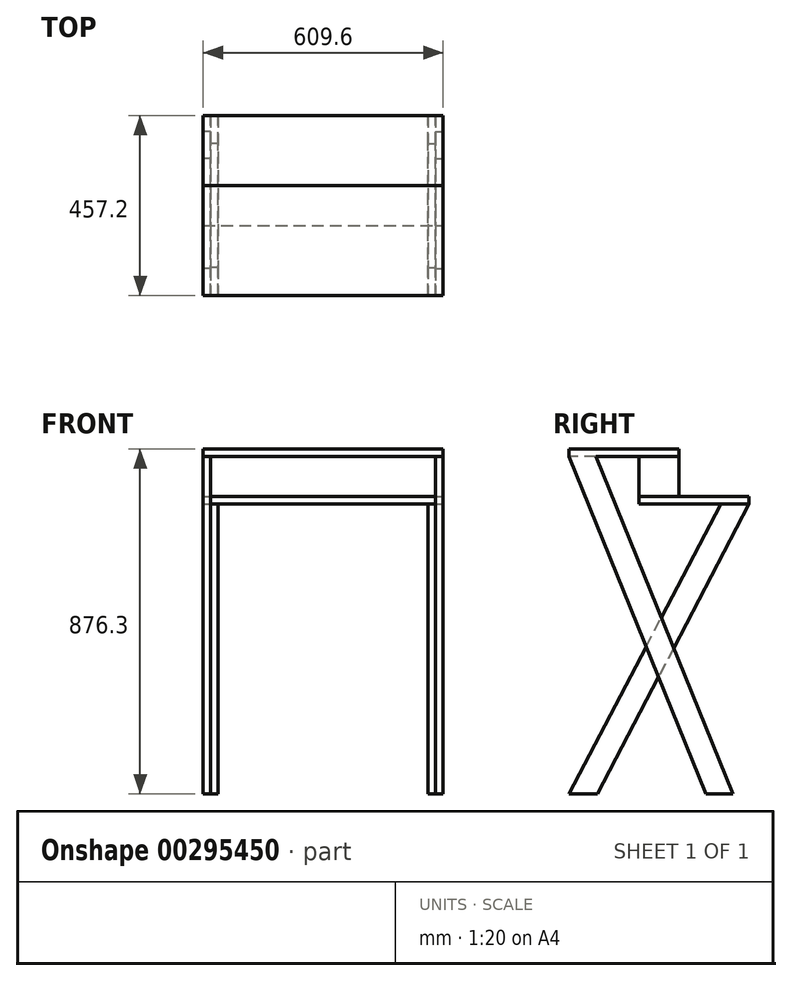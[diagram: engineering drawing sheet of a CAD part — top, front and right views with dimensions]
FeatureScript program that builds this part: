
annotation { "Feature Type Name" : "Feature", "Feature Type Description" : "" }
export const myFeature = defineFeature(function(context is Context, id is Id, definition is map)
    precondition{}
    {
        {
            var Q0;
            Q0=qCreatedBy(makeId("Top.planeOp"),FACE);
            var sketch = newSketch(context, id + "F0", { "sketchPlane" : qUnion([Q0])});
            skLineSegment(sketch, "E0.bottom", {"start": v(0, 0) * mm, "end": v(609.6, 0) * mm});
            skLineSegment(sketch, "E0.top", {"start": v(0, 279.4) * mm, "end": v(609.6, 279.4) * mm});
            skLineSegment(sketch, "E0.left", {"start": v(0, 0) * mm, "end": v(0, 279.4) * mm});
            skLineSegment(sketch, "E0.right", {"start": v(609.6, 0) * mm, "end": v(609.6, 279.4) * mm});
            skSolve(sketch);
        }
        {
            var Q0;
            Q0=makeQuery(id+"F0.imprint","IMPRINT",FACE,{"disambiguationData":[TD([[makeQuery(id+"F0.imprint","IMPRINT",EDGE,{"derivedFrom":sQuery(id+"F0.wireOp",EDGE,"E0.bottom")}),1.0]])]});
            extrude(context, id + "F1", {"entities" : qUnion([Q0]), "depth" : 19.05 * mm});
        }
        {
            var Q0;
            Q0=qCreatedBy(makeId("Top.planeOp"),FACE);
            cPlane(context, id + "F2", {"entities" : qUnion([Q0]), "cplaneType" : CPlaneType.OFFSET, "offset" : 120.65 * mm, "width" : 152.4 * mm, "height" : 152.4 * mm});
        }
        {
            var Q0;
            Q0=qCreatedBy(id+"F2.planeOp",FACE);
            var sketch = newSketch(context, id + "F3", { "sketchPlane" : qUnion([Q0])});
            skLineSegment(sketch, "E1.bottom", {"start": v(0, 101.6) * mm, "end": v(609.6, 101.6) * mm});
            skLineSegment(sketch, "E1.top", {"start": v(0, -177.8) * mm, "end": v(609.6, -177.8) * mm});
            skLineSegment(sketch, "E1.left", {"start": v(0, 101.6) * mm, "end": v(0, -177.8) * mm});
            skLineSegment(sketch, "E1.right", {"start": v(609.6, 101.6) * mm, "end": v(609.6, -177.8) * mm});
            skSolve(sketch);
        }
        {
            var Q0;
            Q0=makeQuery(id+"F3.imprint","IMPRINT",FACE,{"disambiguationData":[TD([[makeQuery(id+"F3.imprint","IMPRINT",EDGE,{"derivedFrom":sQuery(id+"F3.wireOp",EDGE,"E1.bottom")}),-1.0]])]});
            extrude(context, id + "F4", {"entities" : qUnion([Q0]), "depth" : 19.05 * mm});
        }
        {
            var Q0;
            Q0=makeQuery(id+"F4.opExtrude","SWEPT_FACE",FACE,{"disambiguationData":[OSD([sQuery(id+"F3.wireOp",EDGE,"E1.left")])]});
            var sketch = newSketch(context, id + "F5", { "sketchPlane" : qUnion([Q0])});
            skLineSegment(sketch, "E2", {"start": v(177.8, 120.65) * mm, "end": v(-170.08, -736.6) * mm});
            skLineSegment(sketch, "E3", {"start": v(-238.6, -736.6) * mm, "end": v(-170.08, -736.6) * mm});
            skLineSegment(sketch, "E4", {"start": v(-238.6, -736.6) * mm, "end": v(109.27, 120.65) * mm});
            skPoint(sketch, "E5.orphan", {"position": v(177.8, -736.6) * mm});
            skPoint(sketch, "E6.start.orphan", {"position": v(-279.72, 0) * mm});
            skLineSegment(sketch, "E7", {"start": v(109.27, 120.65) * mm, "end": v(177.8, 120.65) * mm});
            skSolve(sketch);
        }
        {
            var Q0;
            Q0=makeQuery(id+"F5.imprint","IMPRINT",FACE,{"disambiguationData":[TD([[makeQuery(id+"F5.imprint","IMPRINT",EDGE,{"derivedFrom":sQuery(id+"F5.wireOp",EDGE,"E2")}),-1.0]])]});
            extrude(context, id + "F6", {"entities" : qUnion([Q0]), "oppositeDirection" : true, "depth" : 19.05 * mm});
        }
        {
            var Q0;
            Q0=makeQuery(id+"F4.opExtrude","SWEPT_FACE",FACE,{"disambiguationData":[OSD([sQuery(id+"F3.wireOp",EDGE,"E1.right")])]});
            var sketch = newSketch(context, id + "F7", { "sketchPlane" : qUnion([Q0])});
            skLineSegment(sketch, "E8.0", {"start": v(238.6, -736.6) * mm, "end": v(-109.27, 120.65) * mm});
            skLineSegment(sketch, "E9.0", {"start": v(238.6, -736.6) * mm, "end": v(170.08, -736.6) * mm});
            skLineSegment(sketch, "E10.0", {"start": v(-177.8, 120.65) * mm, "end": v(170.08, -736.6) * mm});
            skLineSegment(sketch, "E11.0", {"start": v(-109.27, 120.65) * mm, "end": v(-177.8, 120.65) * mm});
            skPoint(sketch, "E12.orphan", {"position": v(101.6, 120.65) * mm});
            skSolve(sketch);
        }
        {
            var Q0;
            Q0=makeQuery(id+"F7.imprint","IMPRINT",FACE,{"disambiguationData":[TD([[makeQuery(id+"F7.imprint","IMPRINT",EDGE,{"derivedFrom":sQuery(id+"F7.wireOp",EDGE,"E8.0")}),1.0]])]});
            extrude(context, id + "F8", {"entities" : qUnion([Q0]), "operationType" : NewBodyOperationType.ADD, "oppositeDirection" : true, "depth" : 19.05 * mm});
        }
        {
            var Q0;
            Q0=makeQuery(id+"F8.opExtrude","CAP_FACE",FACE,{"disambiguationData":[OSD([sQuery(id+"F7.wireOp",EDGE,"E8.0"),sQuery(id+"F7.wireOp",EDGE,"E9.0"),sQuery(id+"F7.wireOp",EDGE,"E10.0"),sQuery(id+"F7.wireOp",EDGE,"E11.0")])],"isStart":false});
            var sketch = newSketch(context, id + "F9", { "sketchPlane" : qUnion([Q0])});
            skLineSegment(sketch, "E13.0", {"start": v(0, 0) * mm, "end": v(-279.4, 0) * mm});
            skLineSegment(sketch, "E14", {"start": v(-279.4, 0) * mm, "end": v(106.13, -736.6) * mm});
            skLineSegment(sketch, "E15", {"start": v(106.13, -736.6) * mm, "end": v(177.8, -736.6) * mm});
            skLineSegment(sketch, "E16", {"start": v(177.8, -736.6) * mm, "end": v(-207.73, 0) * mm});
            skPoint(sketch, "E16.endSnap0", {"position": v(-139.7, 0) * mm});
            skSolve(sketch);
        }
        {
            var Q0;
            Q0 = qSketchRegion(id + "F9", true);
            extrude(context, id + "F10", {"entities" : qUnion([Q0]), "depth" : 19.05 * mm});
        }
        {
            var Q0;
            Q0=makeQuery(id+"F6.opExtrude","CAP_FACE",FACE,{"disambiguationData":[OSD([sQuery(id+"F5.wireOp",EDGE,"E2"),sQuery(id+"F5.wireOp",EDGE,"E3"),sQuery(id+"F5.wireOp",EDGE,"E4"),sQuery(id+"F5.wireOp",EDGE,"E7")])],"isStart":false});
            var sketch = newSketch(context, id + "F11", { "sketchPlane" : qUnion([Q0])});
            skLineSegment(sketch, "E17.0", {"start": v(-177.8, -736.6) * mm, "end": v(207.73, 0) * mm});
            skLineSegment(sketch, "E18.0", {"start": v(-106.13, -736.6) * mm, "end": v(-177.8, -736.6) * mm});
            skLineSegment(sketch, "E19.0", {"start": v(279.4, 0) * mm, "end": v(-106.13, -736.6) * mm});
            skLineSegment(sketch, "E20.0", {"start": v(207.73, 0) * mm, "end": v(279.4, 0) * mm});
            skPoint(sketch, "E21.orphan", {"position": v(0, 0) * mm});
            skSolve(sketch);
        }
        {
            var Q0;
            Q0 = qSketchRegion(id + "F11", true);
            extrude(context, id + "F12", {"entities" : qUnion([Q0]), "depth" : 19.05 * mm});
        }
        {
            var Q0;
            Q0=makeQuery(id+"F1.opExtrude","CAP_FACE",FACE,{"disambiguationData":[OSD([sQuery(id+"F0.wireOp",EDGE,"E0.bottom"),sQuery(id+"F0.wireOp",EDGE,"E0.top"),sQuery(id+"F0.wireOp",EDGE,"E0.left"),sQuery(id+"F0.wireOp",EDGE,"E0.right")])],"isStart":false});
            var sketch = newSketch(context, id + "F13", { "sketchPlane" : qUnion([Q0])});
            skLineSegment(sketch, "E22.0", {"start": v(0, 101.6) * mm, "end": v(0, 0) * mm});
            skLineSegment(sketch, "E23.0", {"start": v(0, 101.6) * mm, "end": v(19.05, 101.6) * mm});
            skLineSegment(sketch, "E24.0", {"start": v(609.6, 101.6) * mm, "end": v(609.6, -177.8) * mm});
            skLineSegment(sketch, "E25", {"start": v(0, 0) * mm, "end": v(19.05, 0) * mm});
            skLineSegment(sketch, "E26", {"start": v(19.05, 0) * mm, "end": v(19.05, 101.6) * mm});
            skPoint(sketch, "E27.orphan", {"position": v(0, -177.8) * mm});
            skLineSegment(sketch, "E28", {"start": v(609.6, 0) * mm, "end": v(590.55, 0) * mm});
            skLineSegment(sketch, "E29", {"start": v(590.55, 0) * mm, "end": v(590.55, 101.6) * mm});
            skLineSegment(sketch, "E30.trimOffspring", {"start": v(590.55, 101.6) * mm, "end": v(609.6, 101.6) * mm});
            skSolve(sketch);
        }
        {
            var Q0;
            Q0 = qSketchRegion(id + "F13", true);
            extrude(context, id + "F14", {"entities" : qUnion([Q0]), "depth" : 101.6 * mm});
        }
    });
